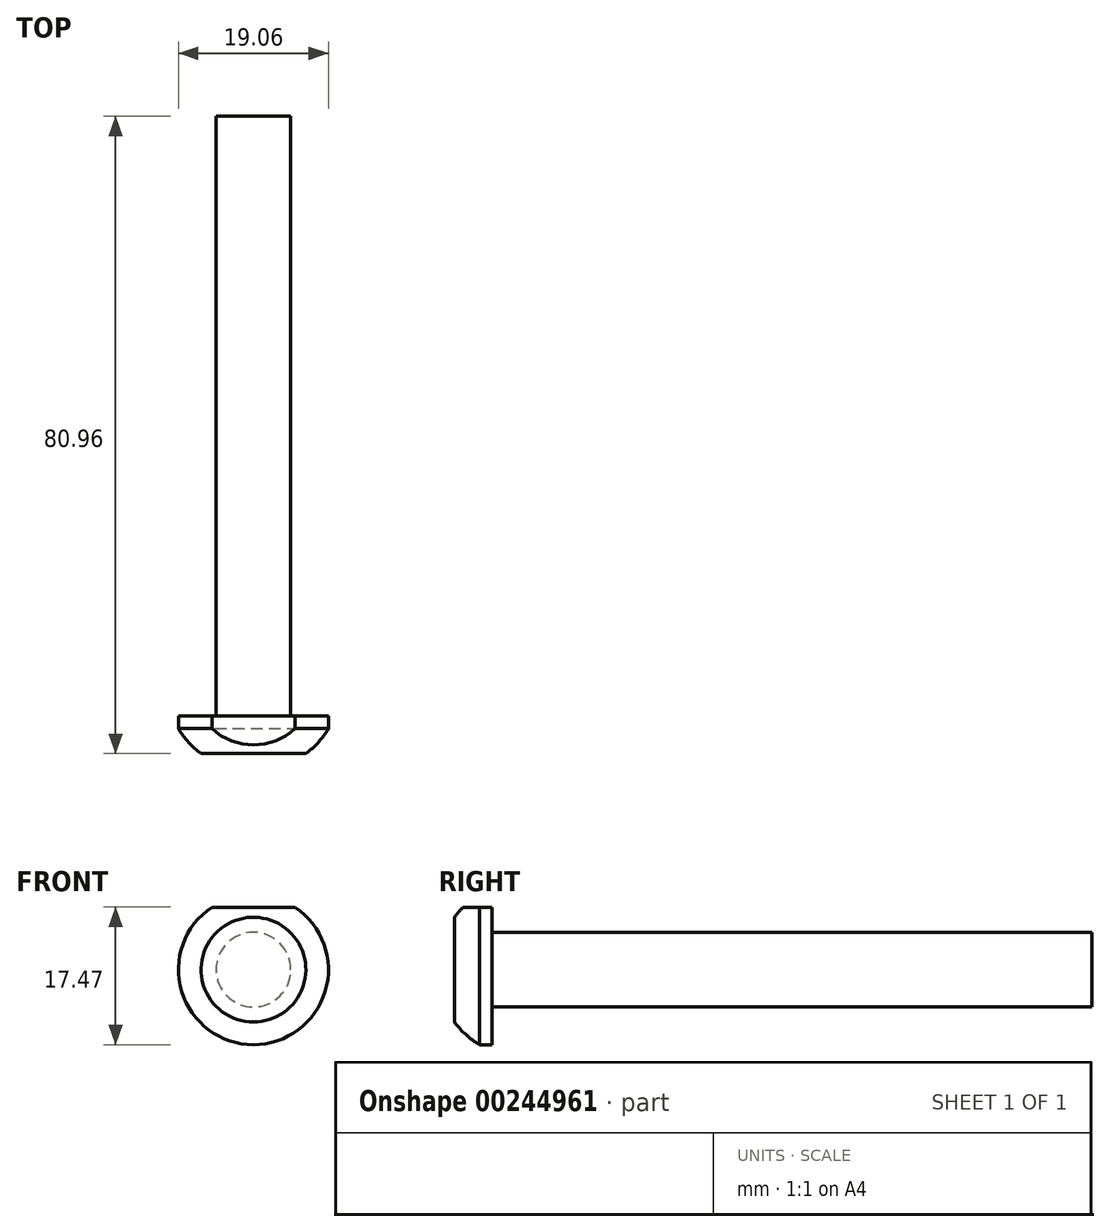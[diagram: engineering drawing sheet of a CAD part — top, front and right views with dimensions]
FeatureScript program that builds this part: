
annotation { "Feature Type Name" : "Feature", "Feature Type Description" : "" }
export const myFeature = defineFeature(function(context is Context, id is Id, definition is map)
    precondition{}
    {
        {
            var Q0;
            Q0=qCreatedBy(makeId("Right.planeOp"),FACE);
            var sketch = newSketch(context, id + "F0", { "sketchPlane" : qUnion([Q0])});
            skLineSegment(sketch, "E0.bottom", {"start": v(0, 0) * mm, "end": v(76.2, 0) * mm});
            skLineSegment(sketch, "E0.top", {"start": v(0, 4.74) * mm, "end": v(76.2, 4.74) * mm});
            skLineSegment(sketch, "E0.right", {"start": v(76.2, 0) * mm, "end": v(76.2, 4.74) * mm});
            skLineSegment(sketch, "E1", {"start": v(0, 4.74) * mm, "end": v(0, 9.53) * mm});
            skLineSegment(sketch, "E2", {"start": v(0, 9.53) * mm, "end": v(-1.59, 9.53) * mm});
            skLineSegment(sketch, "E3", {"start": v(-1.59, 0) * mm, "end": v(0, 0) * mm});
            skArc(sketch, "E4", {"start": v(-1.59, 9.53) * mm, "mid": v(-3.31, 8.24) * mm, "end": v(-4.76, 6.66) * mm});
            skLineSegment(sketch, "E5", {"start": v(-1.59, 0) * mm, "end": v(-4.76, 0) * mm});
            skLineSegment(sketch, "E6", {"start": v(-4.76, 0) * mm, "end": v(-4.76, 6.66) * mm});
            skPoint(sketch, "E7.orphan", {"position": v(-6.98, 0) * mm});
            skSolve(sketch);
        }
        {
            var Q0;
            Q0=makeQuery(id+"F0.imprint","IMPRINT",FACE,{"disambiguationData":[TD([[makeQuery(id+"F0.imprint","IMPRINT",EDGE,{"derivedFrom":sQuery(id+"F0.wireOp",EDGE,"E0.bottom")}),1.0]])]});
            var Q1;
            Q1=sQuery(id+"F0.wireOp",EDGE,"E0.bottom");
            revolve(context, id + "F1", {"entities" : qUnion([Q0]), "axis" : qUnion([Q1]), "revolveType" : RevolveType.FULL});
        }
        {
            var Q0;
            Q0=makeQuery(id+"F1.opRevolve","SWEPT_FACE",FACE,{"disambiguationData":[OSD([sQuery(id+"F0.wireOp",EDGE,"E6")])]});
            var sketch = newSketch(context, id + "F2", { "sketchPlane" : qUnion([Q0])});
            skLineSegment(sketch, "E8", {"start": v(-5.3, 7.94) * mm, "end": v(5.3, 7.94) * mm});
            skArc(sketch, "E9", {"start": v(-5.3, 7.94) * mm, "mid": v(0, 9.54) * mm, "end": v(5.3, 7.94) * mm});
            skPoint(sketch, "E10.orphan", {"position": v(-21.63, 7.94) * mm});
            skPoint(sketch, "E11.orphan", {"position": v(21.63, 7.94) * mm});
            skPoint(sketch, "E12.end.orphan", {"position": v(0, 7.94) * mm});
            skSolve(sketch);
        }
        {
            var Q0;
            Q0=makeQuery(id+"F2.imprint","IMPRINT",FACE,{"disambiguationData":[TD([[makeQuery(id+"F2.imprint","IMPRINT",EDGE,{"derivedFrom":sQuery(id+"F2.wireOp",EDGE,"E8")}),1.0]])]});
            extrude(context, id + "F3", {"entities" : qUnion([Q0]), "operationType" : NewBodyOperationType.REMOVE, "oppositeDirection" : true, "depth" : 4.76 * mm});
        }
    });
